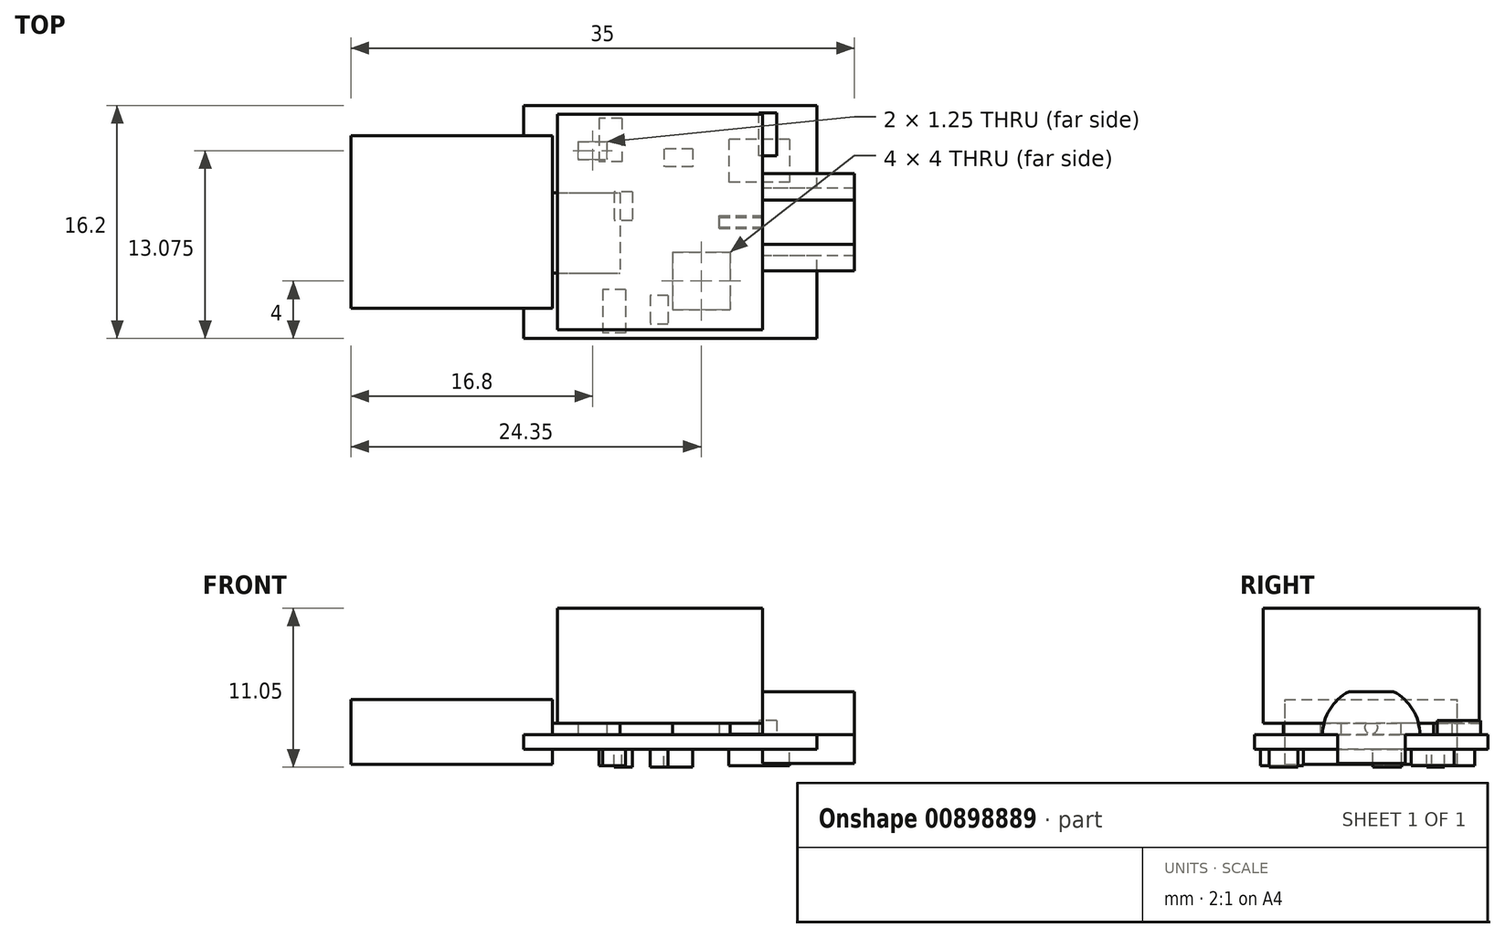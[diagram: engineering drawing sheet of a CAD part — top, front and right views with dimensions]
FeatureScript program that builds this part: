
annotation { "Feature Type Name" : "Feature", "Feature Type Description" : "" }
export const myFeature = defineFeature(function(context is Context, id is Id, definition is map)
    precondition{}
    {
        {
            var Q0;
            Q0=qCreatedBy(makeId("Top.planeOp"),FACE);
            var sketch = newSketch(context, id + "F0", { "sketchPlane" : qUnion([Q0])});
            skLineSegment(sketch, "E0.bottom", {"start": v(10.2, -8.1) * mm, "end": v(-10.2, -8.1) * mm});
            skLineSegment(sketch, "E0.top", {"start": v(10.2, 8.1) * mm, "end": v(-10.2, 8.1) * mm});
            skLineSegment(sketch, "E0.left", {"start": v(10.2, -8.1) * mm, "end": v(10.2, 8.1) * mm});
            skLineSegment(sketch, "E0.right", {"start": v(-10.2, -8.1) * mm, "end": v(-10.2, 8.1) * mm});
            skPoint(sketch, "E0.middle", {"position": v(0, 0) * mm});
            skSolve(sketch);
        }
        {
            var Q0;
            Q0=makeQuery(id+"F0.imprint","IMPRINT",FACE,{"disambiguationData":[TD([[makeQuery(id+"F0.imprint","IMPRINT",EDGE,{"derivedFrom":sQuery(id+"F0.wireOp",EDGE,"E0.bottom")}),-1.0]])]});
            extrude(context, id + "F1", {"entities" : qUnion([Q0]), "oppositeDirection" : true, "depth" : 1 * mm});
        }
        {
            var Q0;
            Q0=makeQuery(id+"F1.opExtrude","SWEPT_FACE",FACE,{"disambiguationData":[OSD([sQuery(id+"F0.wireOp",EDGE,"E0.right")])]});
            var sketch = newSketch(context, id + "F2", { "sketchPlane" : qUnion([Q0])});
            skLineSegment(sketch, "E1.bottom", {"start": v(6, -2.05) * mm, "end": v(-6, -2.05) * mm});
            skLineSegment(sketch, "E1.top", {"start": v(6, 2.45) * mm, "end": v(-6, 2.45) * mm});
            skLineSegment(sketch, "E1.left", {"start": v(6, -2.05) * mm, "end": v(6, 2.45) * mm});
            skLineSegment(sketch, "E1.right", {"start": v(-6, -2.05) * mm, "end": v(-6, 2.45) * mm});
            skPoint(sketch, "E1.middle", {"position": v(0, 0.2) * mm});
            skSolve(sketch);
        }
        {
            var Q0;
            Q0=qSketchRegion(id+"F2",true);
            extrude(context, id + "F3", {"entities" : qUnion([Q0]), "operationType" : NewBodyOperationType.ADD, "depth" : 12 * mm, "hasSecondDirection" : true, "secondDirectionOppositeDirection" : true, "secondDirectionDepth" : 2 * mm});
        }
        {
            var Q0;
            Q0=makeQuery(id+"F1.opExtrude","SWEPT_FACE",FACE,{"disambiguationData":[OSD([sQuery(id+"F0.wireOp",EDGE,"E0.left")])]});
            var sketch = newSketch(context, id + "F4", { "sketchPlane" : qUnion([Q0])});
            skLineSegment(sketch, "E2.top", {"start": v(-2.35, -2) * mm, "end": v(2.35, -2) * mm});
            skLineSegment(sketch, "E2.left", {"start": v(-2.35, 0) * mm, "end": v(-2.35, -2) * mm});
            skLineSegment(sketch, "E2.right", {"start": v(2.35, 0) * mm, "end": v(2.35, -2) * mm});
            skLineSegment(sketch, "E3", {"start": v(0, 0) * mm, "end": v(0, 1.3) * mm, "construction": true});
            skPoint(sketch, "E3.endSnap0", {"position": v(0, 0) * mm});
            skLineSegment(sketch, "E4", {"start": v(-2.35, 0) * mm, "end": v(-3.37, 0) * mm});
            skLineSegment(sketch, "E5", {"start": v(2.35, 0) * mm, "end": v(3.38, 0) * mm});
            skArc(sketch, "E6", {"start": v(3.38, 0) * mm, "mid": v(2.88, 1.76) * mm, "end": v(1.55, 3) * mm});
            skLineSegment(sketch, "E7", {"start": v(-1.55, 3) * mm, "end": v(1.55, 3) * mm});
            skArc(sketch, "E8.trimOffspring", {"start": v(-1.55, 3) * mm, "mid": v(-2.88, 1.76) * mm, "end": v(-3.37, 0) * mm});
            skSolve(sketch);
        }
        {
            var Q0;
            {var subQ0=sQuery(id+"F4.wireOp",EDGE,"E2.top");Q0=makeQuery(id+"F4.imprint","IMPRINT",FACE,{"disambiguationData":[TD([[makeQuery(id+"F4.imprint","IMPRINT",EDGE,{"derivedFrom":subQ0}),1.0]])]});}
            var Q1;
            {var subQ0=sQuery(id+"F4.wireOp",EDGE,"E2.left");var subQ1=sQuery(id+"F0.wireOp",EDGE,"E0.left");var subQ4=makeQuery(id+"F1.opExtrude","CAP_EDGE",EDGE,{"disambiguationData":[OSD([subQ1])],"isStart":false});var subQ5=makeQuery(id+"F4.imprint","INTERSECT",VERTEX,{"derivedFrom":[subQ4,subQ0]});Q1=makeQuery(id+"F4.imprint","IMPRINT",FACE,{"disambiguationData":[TD([[makeQuery(id+"F4.imprint","IMPRINT",EDGE,{"disambiguationData":[TD([[subQ5,-1.0]])],"derivedFrom":subQ4}),1.0]])]});}
            var Q2;
            {var subQ1=sQuery(id+"F4.wireOp",EDGE,"E4");Q2=makeQuery(id+"F4.imprint","IMPRINT",FACE,{"disambiguationData":[TD([[makeQuery(id+"F4.imprint","IMPRINT",EDGE,{"derivedFrom":subQ1}),1.0]])]});}
            extrude(context, id + "F5", {"entities" : qUnion([Q0, Q1, Q2]), "operationType" : NewBodyOperationType.ADD, "depth" : 2.6 * mm, "hasSecondDirection" : true, "secondDirectionOppositeDirection" : true, "secondDirectionDepth" : (6.4 - 2.6) * mm});
        }
        {
            var Q0;
            {var subQ0=sQuery(id+"F4.wireOp",EDGE,"E6");var subQ1=sQuery(id+"F4.wireOp",EDGE,"E7");var subQ2=sQuery(id+"F4.wireOp",EDGE,"E8.trimOffspring");Q0=makeQuery(id+"F5.boolean.opBoolean","SPLIT",FACE,{"disambiguationData":[TD([makeQuery(id+"F5.opExtrude","SWEPT_FACE",FACE,{"disambiguationData":[OSD([subQ0])]})])],"derivedFrom":makeQuery(id+"F5.opExtrude","CAP_FACE",FACE,{"disambiguationData":[OSD([sQuery(id+"F4.wireOp",EDGE,"E2.top"),sQuery(id+"F4.wireOp",EDGE,"E2.left"),sQuery(id+"F4.wireOp",EDGE,"E2.right"),sQuery(id+"F4.wireOp",EDGE,"E4"),sQuery(id+"F4.wireOp",EDGE,"E5"),subQ0,subQ1,subQ2])],"isStart":true})});}
            var sketch = newSketch(context, id + "F6", { "sketchPlane" : qUnion([Q0])});
            skCircle(sketch, "E9", {"center": v(0, 0.5) * mm, "radius": 0.45 * mm});
            skLineSegment(sketch, "E10.0.0", {"start": v(2.35, 0) * mm, "end": v(2.35, -2) * mm, "construction": true});
            skLineSegment(sketch, "E10.0.1", {"start": v(2.35, -2) * mm, "end": v(-2.35, -2) * mm, "construction": true});
            skLineSegment(sketch, "E10.0.2", {"start": v(-2.35, -2) * mm, "end": v(-2.35, 0) * mm, "construction": true});
            skLineSegment(sketch, "E10.0.3", {"start": v(-2.35, 0) * mm, "end": v(-3.38, 0) * mm, "construction": true});
            skArc(sketch, "E10.0.4", {"start": v(-3.38, 0) * mm, "mid": v(-2.88, 1.76) * mm, "end": v(-1.55, 3) * mm, "construction": true});
            skLineSegment(sketch, "E10.0.5", {"start": v(-1.55, 3) * mm, "end": v(1.55, 3) * mm, "construction": true});
            skArc(sketch, "E10.0.6", {"start": v(1.55, 3) * mm, "mid": v(2.88, 1.76) * mm, "end": v(3.37, 0) * mm, "construction": true});
            skLineSegment(sketch, "E10.0.7", {"start": v(3.37, 0) * mm, "end": v(2.35, 0) * mm, "construction": true});
            skCircle(sketch, "E11", {"center": v(0, 0.5) * mm, "radius": 1.73 * mm, "construction": true});
            skLineSegment(sketch, "E12", {"start": v(2.4, 0.5) * mm, "end": v(-2.45, 0.5) * mm, "construction": true});
            skSolve(sketch);
        }
        {
            var Q0;
            Q0=qSketchRegion(id+"F6",true);
            extrude(context, id + "F7", {"entities" : qUnion([Q0]), "operationType" : NewBodyOperationType.ADD, "depth" : 3 * mm});
        }
        {
            var Q0;
            Q0=makeQuery(id+"F1.opExtrude","CAP_FACE",FACE,{"disambiguationData":[OSD([sQuery(id+"F0.wireOp",EDGE,"E0.bottom"),sQuery(id+"F0.wireOp",EDGE,"E0.top"),sQuery(id+"F0.wireOp",EDGE,"E0.left"),sQuery(id+"F0.wireOp",EDGE,"E0.right")])],"isStart":true});
            var sketch = newSketch(context, id + "F8", { "sketchPlane" : qUnion([Q0])});
            skLineSegment(sketch, "E13.bottom", {"start": v(-9.1, 2.05) * mm, "end": v(-3.5, 2.05) * mm});
            skLineSegment(sketch, "E13.top", {"start": v(-9.1, -3.55) * mm, "end": v(-3.5, -3.55) * mm});
            skLineSegment(sketch, "E13.left", {"start": v(-9.1, 2.05) * mm, "end": v(-9.1, -3.55) * mm});
            skLineSegment(sketch, "E13.right", {"start": v(-3.5, 2.05) * mm, "end": v(-3.5, -3.55) * mm});
            skSolve(sketch);
        }
        {
            var Q0;
            Q0=qSketchRegion(id+"F8",true);
            extrude(context, id + "F9", {"entities" : qUnion([Q0]), "operationType" : NewBodyOperationType.ADD, "depth" : .8 * mm});
        }
        {
            var Q0;
            Q0=makeQuery(id+"F1.opExtrude","CAP_FACE",FACE,{"disambiguationData":[OSD([sQuery(id+"F0.wireOp",EDGE,"E0.bottom"),sQuery(id+"F0.wireOp",EDGE,"E0.top"),sQuery(id+"F0.wireOp",EDGE,"E0.left"),sQuery(id+"F0.wireOp",EDGE,"E0.right")])],"isStart":true});
            var sketch = newSketch(context, id + "F10", { "sketchPlane" : qUnion([Q0])});
            skLineSegment(sketch, "E14.bottom", {"start": v(0.15, -2.1) * mm, "end": v(4.15, -2.1) * mm});
            skLineSegment(sketch, "E14.top", {"start": v(0.15, -6.1) * mm, "end": v(4.15, -6.1) * mm});
            skLineSegment(sketch, "E14.left", {"start": v(0.15, -2.1) * mm, "end": v(0.15, -6.1) * mm});
            skLineSegment(sketch, "E14.right", {"start": v(4.15, -2.1) * mm, "end": v(4.15, -6.1) * mm});
            skSolve(sketch);
        }
        {
            var Q0;
            Q0=qSketchRegion(id+"F10",true);
            extrude(context, id + "F11", {"entities" : qUnion([Q0]), "operationType" : NewBodyOperationType.ADD, "depth" : .8 * mm});
        }
        {
            var Q0;
            Q0=makeQuery(id+"F1.opExtrude","CAP_FACE",FACE,{"disambiguationData":[OSD([sQuery(id+"F0.wireOp",EDGE,"E0.bottom"),sQuery(id+"F0.wireOp",EDGE,"E0.top"),sQuery(id+"F0.wireOp",EDGE,"E0.left"),sQuery(id+"F0.wireOp",EDGE,"E0.right")])],"isStart":true});
            var sketch = newSketch(context, id + "F12", { "sketchPlane" : qUnion([Q0])});
            skLineSegment(sketch, "E15.bottom", {"start": v(-6.4, 5.6) * mm, "end": v(-4.4, 5.6) * mm});
            skLineSegment(sketch, "E15.top", {"start": v(-6.4, 4.35) * mm, "end": v(-4.4, 4.35) * mm});
            skLineSegment(sketch, "E15.left", {"start": v(-6.4, 5.6) * mm, "end": v(-6.4, 4.35) * mm});
            skLineSegment(sketch, "E15.right", {"start": v(-4.4, 5.6) * mm, "end": v(-4.4, 4.35) * mm});
            skSolve(sketch);
        }
        {
            var Q0;
            Q0=qSketchRegion(id+"F12",true);
            extrude(context, id + "F13", {"entities" : qUnion([Q0]), "operationType" : NewBodyOperationType.ADD, "depth" : 1.25 * mm});
        }
        {
            var Q0;
            Q0=makeQuery(id+"F12.imprint","IMPRINT",FACE,{"disambiguationData":[TD([[makeQuery(id+"F12.imprint","IMPRINT",EDGE,{"derivedFrom":sQuery(id+"F12.wireOp",EDGE,"E15.bottom")}),1.0]])]});
            var sketch = newSketch(context, id + "F14", { "sketchPlane" : qUnion([Q0])});
            skLineSegment(sketch, "E16.bottom", {"start": v(7.4, 4.6) * mm, "end": v(6.15, 4.6) * mm});
            skLineSegment(sketch, "E16.top", {"start": v(7.4, 7.6) * mm, "end": v(6.15, 7.6) * mm});
            skLineSegment(sketch, "E16.left", {"start": v(7.4, 4.6) * mm, "end": v(7.4, 7.6) * mm});
            skLineSegment(sketch, "E16.right", {"start": v(6.15, 4.6) * mm, "end": v(6.15, 7.6) * mm});
            skSolve(sketch);
        }
        {
            var Q0;
            Q0=qSketchRegion(id+"F14",true);
            extrude(context, id + "F15", {"entities" : qUnion([Q0]), "operationType" : NewBodyOperationType.ADD, "depth" : 1 * mm});
        }
        {
            var Q0;
            Q0=makeQuery(id+"F1.opExtrude","CAP_FACE",FACE,{"disambiguationData":[OSD([sQuery(id+"F0.wireOp",EDGE,"E0.bottom"),sQuery(id+"F0.wireOp",EDGE,"E0.top"),sQuery(id+"F0.wireOp",EDGE,"E0.left"),sQuery(id+"F0.wireOp",EDGE,"E0.right")])],"isStart":false});
            var sketch = newSketch(context, id + "F16", { "sketchPlane" : qUnion([Q0])});
            skLineSegment(sketch, "E17.bottom", {"start": v(1.55, -5.1) * mm, "end": v(-0.45, -5.1) * mm});
            skLineSegment(sketch, "E17.top", {"start": v(1.55, -3.85) * mm, "end": v(-0.45, -3.85) * mm});
            skLineSegment(sketch, "E17.left", {"start": v(1.55, -5.1) * mm, "end": v(1.55, -3.85) * mm});
            skLineSegment(sketch, "E17.right", {"start": v(-0.45, -5.1) * mm, "end": v(-0.45, -3.85) * mm});
            skLineSegment(sketch, "E18.bottom", {"start": v(-2.65, -2.1) * mm, "end": v(-3.9, -2.1) * mm});
            skLineSegment(sketch, "E18.top", {"start": v(-2.65, -0.1) * mm, "end": v(-3.9, -0.1) * mm});
            skLineSegment(sketch, "E18.left", {"start": v(-2.65, -2.1) * mm, "end": v(-2.65, -0.1) * mm});
            skLineSegment(sketch, "E18.right", {"start": v(-3.9, -2.1) * mm, "end": v(-3.9, -0.1) * mm});
            skLineSegment(sketch, "E19.bottom", {"start": v(-0.15, 5.1) * mm, "end": v(-1.4, 5.1) * mm});
            skLineSegment(sketch, "E19.top", {"start": v(-0.15, 7.1) * mm, "end": v(-1.4, 7.1) * mm});
            skLineSegment(sketch, "E19.left", {"start": v(-0.15, 5.1) * mm, "end": v(-0.15, 7.1) * mm});
            skLineSegment(sketch, "E19.right", {"start": v(-1.4, 5.1) * mm, "end": v(-1.4, 7.1) * mm});
            skSolve(sketch);
        }
        {
            var Q0;
            Q0=qSketchRegion(id+"F16",true);
            extrude(context, id + "F17", {"entities" : qUnion([Q0]), "operationType" : NewBodyOperationType.ADD, "depth" : 1.25 * mm});
        }
        {
            var Q0;
            Q0=makeQuery(id+"F1.opExtrude","CAP_FACE",FACE,{"disambiguationData":[OSD([sQuery(id+"F0.wireOp",EDGE,"E0.bottom"),sQuery(id+"F0.wireOp",EDGE,"E0.top"),sQuery(id+"F0.wireOp",EDGE,"E0.left"),sQuery(id+"F0.wireOp",EDGE,"E0.right")])],"isStart":false});
            var sketch = newSketch(context, id + "F18", { "sketchPlane" : qUnion([Q0])});
            skLineSegment(sketch, "E20.bottom", {"start": v(-3.35, -7.2) * mm, "end": v(-4.95, -7.2) * mm});
            skLineSegment(sketch, "E20.top", {"start": v(-3.35, -4.2) * mm, "end": v(-4.95, -4.2) * mm});
            skLineSegment(sketch, "E20.left", {"start": v(-3.35, -7.2) * mm, "end": v(-3.35, -4.2) * mm});
            skLineSegment(sketch, "E20.right", {"start": v(-4.95, -7.2) * mm, "end": v(-4.95, -4.2) * mm});
            skLineSegment(sketch, "E21.bottom", {"start": v(-3.1, 4.7) * mm, "end": v(-4.7, 4.7) * mm});
            skLineSegment(sketch, "E21.top", {"start": v(-3.1, 7.7) * mm, "end": v(-4.7, 7.7) * mm});
            skLineSegment(sketch, "E21.left", {"start": v(-3.1, 4.7) * mm, "end": v(-3.1, 7.7) * mm});
            skLineSegment(sketch, "E21.right", {"start": v(-4.7, 4.7) * mm, "end": v(-4.7, 7.7) * mm});
            skSolve(sketch);
        }
        {
            var Q0;
            Q0=qSketchRegion(id+"F18",true);
            extrude(context, id + "F19", {"entities" : qUnion([Q0]), "operationType" : NewBodyOperationType.ADD, "depth" : 1.15 * mm});
        }
        {
            var Q0;
            Q0=makeQuery(id+"F1.opExtrude","CAP_FACE",FACE,{"disambiguationData":[OSD([sQuery(id+"F0.wireOp",EDGE,"E0.bottom"),sQuery(id+"F0.wireOp",EDGE,"E0.top"),sQuery(id+"F0.wireOp",EDGE,"E0.left"),sQuery(id+"F0.wireOp",EDGE,"E0.right")])],"isStart":false});
            var sketch = newSketch(context, id + "F20", { "sketchPlane" : qUnion([Q0])});
            skLineSegment(sketch, "E22.bottom", {"start": v(8.3, -5.77) * mm, "end": v(4.05, -5.77) * mm});
            skLineSegment(sketch, "E22.top", {"start": v(8.3, -2.77) * mm, "end": v(4.05, -2.77) * mm});
            skLineSegment(sketch, "E22.left", {"start": v(8.3, -5.77) * mm, "end": v(8.3, -2.77) * mm});
            skLineSegment(sketch, "E22.right", {"start": v(4.05, -5.77) * mm, "end": v(4.05, -2.77) * mm});
            skSolve(sketch);
        }
        {
            var Q0;
            Q0=qSketchRegion(id+"F20",true);
            extrude(context, id + "F21", {"entities" : qUnion([Q0]), "operationType" : NewBodyOperationType.ADD, "depth" : 1.15 * mm});
        }
        {
            var Q0;
            Q0=makeQuery(id+"F9.opExtrude","CAP_FACE",FACE,{"disambiguationData":[OSD([sQuery(id+"F8.wireOp",EDGE,"E13.bottom"),sQuery(id+"F8.wireOp",EDGE,"E13.top"),sQuery(id+"F8.wireOp",EDGE,"E13.left"),sQuery(id+"F8.wireOp",EDGE,"E13.right")])],"isStart":false});
            var sketch = newSketch(context, id + "F22", { "sketchPlane" : qUnion([Q0])});
            skLineSegment(sketch, "E23.bottom", {"start": v(-7.85, 7.5) * mm, "end": v(6.4, 7.5) * mm});
            skLineSegment(sketch, "E23.top", {"start": v(-7.85, -7.5) * mm, "end": v(6.4, -7.5) * mm});
            skLineSegment(sketch, "E23.left", {"start": v(-7.85, 7.5) * mm, "end": v(-7.85, -7.5) * mm});
            skLineSegment(sketch, "E23.right", {"start": v(6.4, 7.5) * mm, "end": v(6.4, -7.5) * mm});
            skLineSegment(sketch, "E24", {"start": v(12.8, 0) * mm, "end": v(-17.3, 0) * mm, "construction": true});
            skSolve(sketch);
        }
        {
            var Q0;
            Q0=qSketchRegion(id+"F22",true);
            extrude(context, id + "F23", {"entities" : qUnion([Q0]), "operationType" : NewBodyOperationType.ADD, "depth" : 8 * mm, "offsetDistance" : 25 * mm});
        }
    });
